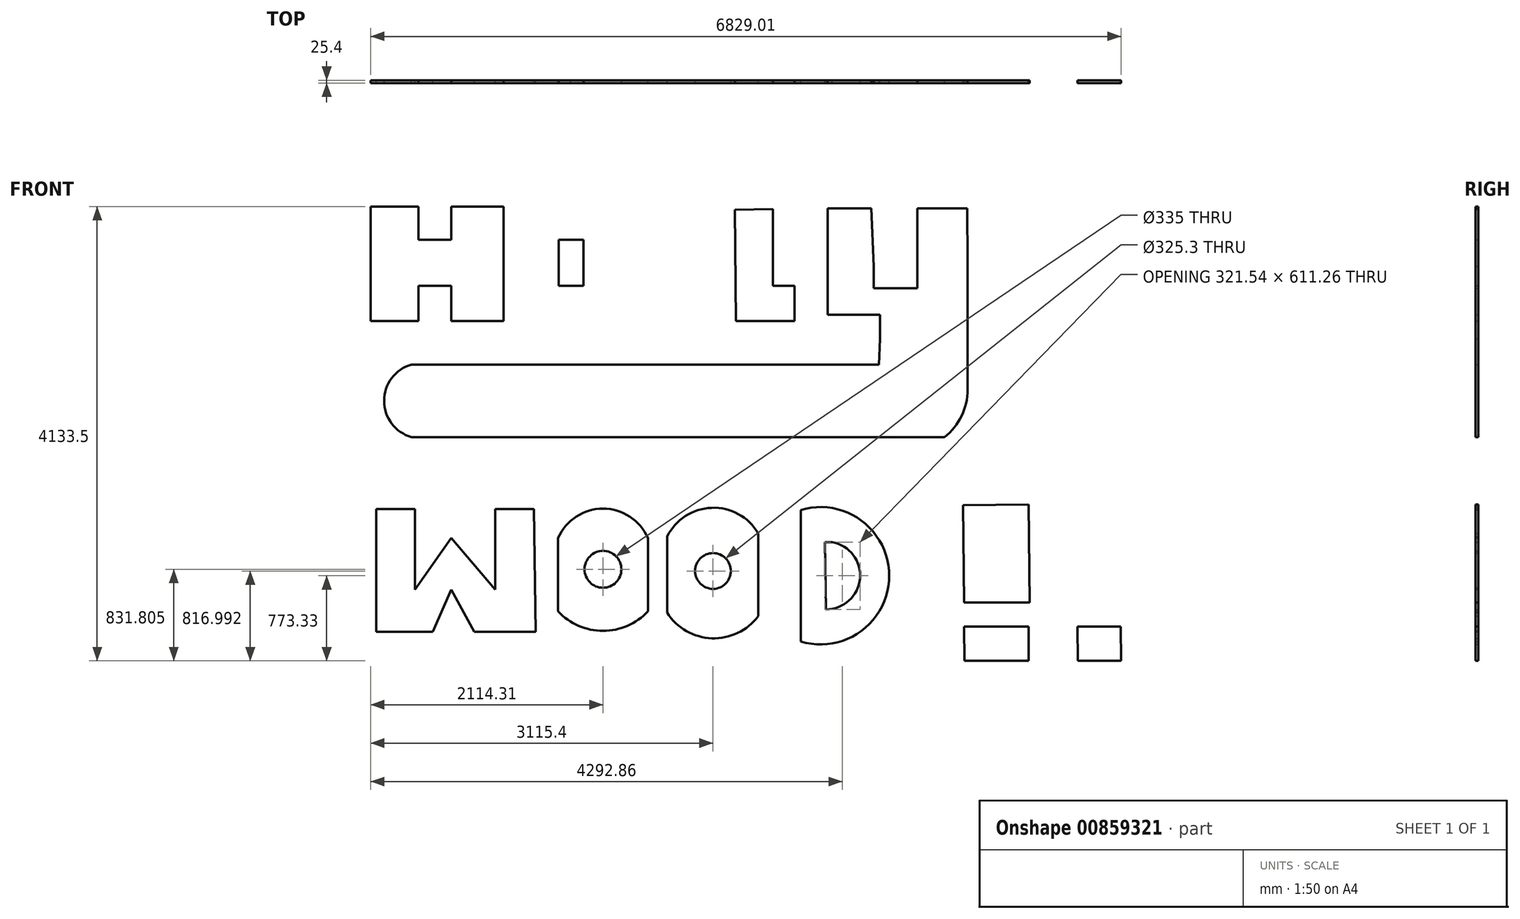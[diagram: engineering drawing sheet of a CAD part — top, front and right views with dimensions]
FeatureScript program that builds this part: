
annotation { "Feature Type Name" : "Feature", "Feature Type Description" : "" }
export const myFeature = defineFeature(function(context is Context, id is Id, definition is map)
    precondition{}
    {
        {
            var Q0;
            Q0=qCreatedBy(makeId("Front.planeOp"),FACE);
            var sketch = newSketch(context, id + "F0", { "sketchPlane" : qUnion([Q0])});
            skLineSegment(sketch, "E0.bottom", {"start": v(0, 0) * mm, "end": v(7620, 0) * mm, "construction": true});
            skLineSegment(sketch, "E0.top", {"start": v(0, 5080) * mm, "end": v(7620, 5080) * mm, "construction": true});
            skLineSegment(sketch, "E0.left", {"start": v(0, 0) * mm, "end": v(0, 5080) * mm, "construction": true});
            skLineSegment(sketch, "E0.right", {"start": v(7620, 0) * mm, "end": v(7620, 5080) * mm, "construction": true});
            skLineSegment(sketch, "E1", {"start": v(329.04, 4613.24) * mm, "end": v(329.04, 3602.22) * mm});
            skLineSegment(sketch, "E2", {"start": v(329.04, 3602.22) * mm, "end": v(763.28, 3602.22) * mm});
            skLineSegment(sketch, "E3", {"start": v(763.28, 3602.22) * mm, "end": v(763.28, 3922.7) * mm});
            skLineSegment(sketch, "E4", {"start": v(763.28, 3922.7) * mm, "end": v(1063.6, 3922.7) * mm});
            skLineSegment(sketch, "E5", {"start": v(1063.6, 3922.7) * mm, "end": v(1063.6, 3602.22) * mm});
            skLineSegment(sketch, "E6", {"start": v(1063.6, 3602.22) * mm, "end": v(1539.88, 3602.22) * mm});
            skLineSegment(sketch, "E7", {"start": v(1539.88, 3602.22) * mm, "end": v(1539.88, 4642.67) * mm});
            skLineSegment(sketch, "E8", {"start": v(1539.88, 4642.67) * mm, "end": v(1063.6, 4642.67) * mm});
            skLineSegment(sketch, "E9", {"start": v(1063.6, 4642.67) * mm, "end": v(1063.6, 4342.18) * mm});
            skLineSegment(sketch, "E10", {"start": v(1063.6, 4342.18) * mm, "end": v(763.28, 4342.18) * mm});
            skLineSegment(sketch, "E11", {"start": v(763.28, 4342.18) * mm, "end": v(763.28, 4642.67) * mm});
            skLineSegment(sketch, "E12", {"start": v(1842.03, 4642.67) * mm, "end": v(1842.03, 3602.22) * mm});
            skLineSegment(sketch, "E13", {"start": v(1842.03, 3602.22) * mm, "end": v(2455.63, 3602.22) * mm});
            skLineSegment(sketch, "E14", {"start": v(2455.63, 4613.24) * mm, "end": v(2455.63, 3602.22) * mm});
            skLineSegment(sketch, "E15", {"start": v(2757.78, 4613.24) * mm, "end": v(2757.78, 3602.22) * mm});
            skLineSegment(sketch, "E16", {"start": v(2757.78, 3602.22) * mm, "end": v(3291.75, 3602.22) * mm});
            skLineSegment(sketch, "E17", {"start": v(3291.75, 3602.22) * mm, "end": v(3291.75, 3922.7) * mm});
            skLineSegment(sketch, "E18", {"start": v(3291.75, 3922.7) * mm, "end": v(3034.26, 3922.7) * mm});
            skLineSegment(sketch, "E19", {"start": v(3034.26, 3922.7) * mm, "end": v(3034.26, 4613.24) * mm});
            skLineSegment(sketch, "E20", {"start": v(3653.43, 3602.22) * mm, "end": v(4187.93, 3602.22) * mm});
            skLineSegment(sketch, "E21", {"start": v(4187.93, 3602.22) * mm, "end": v(4187.93, 3922.7) * mm});
            skLineSegment(sketch, "E22", {"start": v(4187.93, 3922.7) * mm, "end": v(3990.16, 3922.7) * mm});
            skLineSegment(sketch, "E23", {"start": v(3990.16, 3922.7) * mm, "end": v(3990.16, 4620.52) * mm});
            skLineSegment(sketch, "E24", {"start": v(3990.16, 4620.52) * mm, "end": v(3644.03, 4613.24) * mm});
            skLineSegment(sketch, "E25", {"start": v(4488.18, 4136.58) * mm, "end": v(4488.18, 3658.5) * mm});
            skLineSegment(sketch, "E26", {"start": v(4488.18, 3658.5) * mm, "end": v(4964.46, 3658.5) * mm});
            skLineSegment(sketch, "E27", {"start": v(4906.11, 4098.37) * mm, "end": v(4906.11, 3899.15) * mm});
            skLineSegment(sketch, "E28", {"start": v(4906.11, 3899.15) * mm, "end": v(5303.61, 3899.15) * mm});
            skLineSegment(sketch, "E29", {"start": v(5303.61, 3899.15) * mm, "end": v(5303.61, 4136.58) * mm});
            skLineSegment(sketch, "E30", {"start": v(5762.28, 4136.58) * mm, "end": v(5762.28, 3364.67) * mm});
            skLineSegment(sketch, "E31", {"start": v(4964.46, 3658.5) * mm, "end": v(4964.46, 3364.67) * mm});
            skLineSegment(sketch, "E32", {"start": v(4940.82, 2544.55) * mm, "end": v(701, 2544.55) * mm});
            skFitSpline(sketch, "E33", {"points": [v(501.66, 2544.55) * mm, v(461.58, 2544.55) * mm], "startDerivative": vector(-40.08, 0) * mm, "endDerivative": vector(-40.08, 0) * mm});
            skLineSegment(sketch, "E34", {"start": v(700.01, 3205.4) * mm, "end": v(4485.04, 3205.4) * mm});
            skLineSegment(sketch, "E35", {"start": v(379.86, 1889.1) * mm, "end": v(379.86, 773.5) * mm});
            skLineSegment(sketch, "E36", {"start": v(379.86, 773.5) * mm, "end": v(893.66, 773.5) * mm});
            skLineSegment(sketch, "E37", {"start": v(1273.15, 773.5) * mm, "end": v(1829.45, 773.5) * mm});
            skLineSegment(sketch, "E38", {"start": v(1061.78, 1157.75) * mm, "end": v(893.66, 773.5) * mm});
            skLineSegment(sketch, "E39", {"start": v(1061.78, 1157.75) * mm, "end": v(1273.15, 773.5) * mm});
            skLineSegment(sketch, "E40", {"start": v(379.86, 1889.1) * mm, "end": v(731.2, 1889.1) * mm});
            skLineSegment(sketch, "E41", {"start": v(731.2, 1889.1) * mm, "end": v(731.2, 1157.75) * mm});
            skLineSegment(sketch, "E42", {"start": v(731.2, 1157.75) * mm, "end": v(1061.78, 1625.55) * mm});
            skLineSegment(sketch, "E43", {"start": v(1061.78, 1625.55) * mm, "end": v(1460.97, 1157.75) * mm});
            skLineSegment(sketch, "E44", {"start": v(1460.97, 1157.75) * mm, "end": v(1460.97, 1889.1) * mm});
            skLineSegment(sketch, "E45", {"start": v(1460.97, 1889.1) * mm, "end": v(1816.5, 1889.1) * mm});
            skLineSegment(sketch, "E46", {"start": v(1816.5, 1889.1) * mm, "end": v(1829.45, 773.5) * mm});
            skLineSegment(sketch, "E47", {"start": v(2034.8, 1625.55) * mm, "end": v(2034.8, 958.16) * mm});
            skLineSegment(sketch, "E48", {"start": v(2851.9, 1625.55) * mm, "end": v(2851.9, 958.16) * mm});
            skArc(sketch, "E49", {"start": v(2851.9, 1625.55) * mm, "mid": v(2443.35, 1893.8) * mm, "end": v(2034.8, 1625.55) * mm});
            skArc(sketch, "E50", {"start": v(2034.8, 958.16) * mm, "mid": v(2443.35, 781.1) * mm, "end": v(2851.9, 958.16) * mm});
            skCircle(sketch, "E51", {"center": v(2443.35, 1340.97) * mm, "radius": 167.5 * mm});
            skLineSegment(sketch, "E52", {"start": v(3026.54, 1638.03) * mm, "end": v(3026.54, 945.68) * mm});
            skLineSegment(sketch, "E53", {"start": v(3856.1, 1669.22) * mm, "end": v(3856.1, 914.5) * mm});
            skArc(sketch, "E54", {"start": v(3856.1, 1669.22) * mm, "mid": v(3432.02, 1901.07) * mm, "end": v(3026.54, 1638.03) * mm});
            skArc(sketch, "E55", {"start": v(3026.54, 945.68) * mm, "mid": v(3433.17, 713.36) * mm, "end": v(3856.1, 914.5) * mm});
            skCircle(sketch, "E56", {"center": v(3444.44, 1326.16) * mm, "radius": 162.65 * mm});
            skLineSegment(sketch, "E57", {"start": v(4242.82, 1881.28) * mm, "end": v(4242.82, 683.72) * mm});
            skArc(sketch, "E58", {"start": v(4242.82, 683.72) * mm, "mid": v(5047.53, 1282.5) * mm, "end": v(4242.82, 1881.28) * mm});
            skLineSegment(sketch, "E59", {"start": v(4461.13, 1588.13) * mm, "end": v(4473.6, 976.87) * mm});
            skArc(sketch, "E60", {"start": v(4473.6, 976.87) * mm, "mid": v(4782.67, 1256.7) * mm, "end": v(4529.74, 1588.13) * mm});
            skLineSegment(sketch, "E61", {"start": v(763.28, 4642.67) * mm, "end": v(329.04, 4642.67) * mm});
            skLineSegment(sketch, "E62", {"start": v(329.04, 4642.67) * mm, "end": v(329.04, 4613.24) * mm});
            skLineSegment(sketch, "E63", {"start": v(1842.03, 4642.67) * mm, "end": v(2455.63, 4642.67) * mm});
            skLineSegment(sketch, "E64", {"start": v(2745.86, 4638.19) * mm, "end": v(3034.26, 4638.19) * mm});
            skLineSegment(sketch, "E65", {"start": v(3644.03, 4613.24) * mm, "end": v(3653.43, 3602.22) * mm});
            skLineSegment(sketch, "E66", {"start": v(4488.18, 4136.58) * mm, "end": v(4488.18, 4625.71) * mm});
            skLineSegment(sketch, "E67", {"start": v(4488.18, 4625.71) * mm, "end": v(4885.26, 4625.71) * mm});
            skLineSegment(sketch, "E68", {"start": v(4885.26, 4625.71) * mm, "end": v(4906.11, 4098.37) * mm});
            skLineSegment(sketch, "E69", {"start": v(5303.61, 4136.58) * mm, "end": v(5303.61, 4625.71) * mm});
            skLineSegment(sketch, "E70", {"start": v(5303.61, 4625.71) * mm, "end": v(5758.5, 4625.71) * mm});
            skLineSegment(sketch, "E71", {"start": v(5758.5, 4625.71) * mm, "end": v(5762.28, 4136.58) * mm});
            skLineSegment(sketch, "E72", {"start": v(4485.04, 3205.4) * mm, "end": v(4953.88, 3205.4) * mm});
            skLineSegment(sketch, "E73", {"start": v(4953.88, 3205.4) * mm, "end": v(4964.46, 3440.62) * mm});
            skLineSegment(sketch, "E74", {"start": v(700.01, 3205.4) * mm, "end": v(700.01, 3141.23) * mm});
            skLineSegment(sketch, "E75", {"start": v(5762.28, 3364.67) * mm, "end": v(5762.28, 2979.06) * mm});
            skLineSegment(sketch, "E76", {"start": v(4940.82, 2544.55) * mm, "end": v(5552.66, 2544.55) * mm});
            skArc(sketch, "E77", {"start": v(5552.66, 2544.55) * mm, "mid": v(5707.13, 2737.84) * mm, "end": v(5762.28, 2979.06) * mm});
            skArc(sketch, "E78", {"start": v(700.01, 3205.4) * mm, "mid": v(451.24, 2874.6) * mm, "end": v(701, 2544.55) * mm});
            skLineSegment(sketch, "E79", {"start": v(4529.74, 1588.13) * mm, "end": v(4461.13, 1588.13) * mm});
            skLineSegment(sketch, "E80", {"start": v(2148.83, 4342.18) * mm, "end": v(2266.03, 4342.18) * mm});
            skLineSegment(sketch, "E81", {"start": v(2266.03, 4342.18) * mm, "end": v(2266.03, 3922.7) * mm});
            skLineSegment(sketch, "E82", {"start": v(2266.03, 3922.7) * mm, "end": v(2148.83, 3922.7) * mm});
            skLineSegment(sketch, "E83", {"start": v(2148.83, 4342.18) * mm, "end": v(2041.49, 4342.18) * mm});
            skLineSegment(sketch, "E84", {"start": v(2041.49, 4342.18) * mm, "end": v(2041.49, 3920.9) * mm});
            skLineSegment(sketch, "E85", {"start": v(2041.49, 3920.9) * mm, "end": v(2148.83, 3922.7) * mm});
            skLineSegment(sketch, "E86", {"start": v(5721.52, 1924.95) * mm, "end": v(5729.75, 1039.55) * mm});
            skLineSegment(sketch, "E87", {"start": v(5729.75, 1039.55) * mm, "end": v(6326.54, 1039.55) * mm});
            skLineSegment(sketch, "E88", {"start": v(6326.54, 1039.55) * mm, "end": v(6318.25, 1931.63) * mm});
            skLineSegment(sketch, "E89", {"start": v(6318.25, 1931.63) * mm, "end": v(5721.52, 1924.95) * mm});
            skLineSegment(sketch, "E90", {"start": v(5729.75, 820.94) * mm, "end": v(5732.65, 509.17) * mm});
            skLineSegment(sketch, "E91", {"start": v(5732.65, 509.17) * mm, "end": v(6318.25, 509.17) * mm});
            skLineSegment(sketch, "E92", {"start": v(6318.25, 509.17) * mm, "end": v(6315.35, 820.78) * mm});
            skLineSegment(sketch, "E93", {"start": v(6315.35, 820.78) * mm, "end": v(5729.75, 820.94) * mm});
            skLineSegment(sketch, "E94", {"start": v(6628.8, 1924.95) * mm, "end": v(6638.71, 1039.55) * mm});
            skLineSegment(sketch, "E95", {"start": v(6638.71, 1039.55) * mm, "end": v(7158.05, 1039.55) * mm});
            skLineSegment(sketch, "E96", {"start": v(7158.05, 1039.55) * mm, "end": v(7148.14, 1924.95) * mm});
            skLineSegment(sketch, "E97", {"start": v(7140.4, 1887.52) * mm, "end": v(6628.8, 1924.95) * mm});
            skLineSegment(sketch, "E98", {"start": v(6761.11, 820.78) * mm, "end": v(6764.6, 509.17) * mm});
            skLineSegment(sketch, "E99", {"start": v(6764.6, 509.17) * mm, "end": v(7158.05, 509.17) * mm});
            skLineSegment(sketch, "E100", {"start": v(7158.05, 509.17) * mm, "end": v(7154.56, 820.78) * mm});
            skLineSegment(sketch, "E101", {"start": v(7154.56, 820.78) * mm, "end": v(6761.11, 820.78) * mm});
            skSolve(sketch);
        }
        {
            var Q0;
            Q0=qCreatedBy(makeId("Front.planeOp"),FACE);
            var sketch = newSketch(context, id + "F1", { "sketchPlane" : qUnion([Q0])});
            skLineSegment(sketch, "E102", {"start": v(1828.97, 771.04) * mm, "end": v(1828.97, 1893.76) * mm});
            skSolve(sketch);
        }
        {
            var Q0;
            Q0=qCreatedBy(makeId("Front.planeOp"),FACE);
            var sketch = newSketch(context, id + "F2", { "sketchPlane" : qUnion([Q0])});
            skSolve(sketch);
        }
        {
            var Q0;
            Q0 = qSketchRegion(id + "F0", true);
            var Q1;
            Q1 = qSketchRegion(id + "F1", true);
            var Q2;
            Q2 = qSketchRegion(id + "F2", true);
            extrude(context, id + "F3", {"entities" : qUnion([Q0, Q1, Q2]), "depth" : 25.4 * mm, "offsetDistance" : 25.4 * mm});
        }
    });
